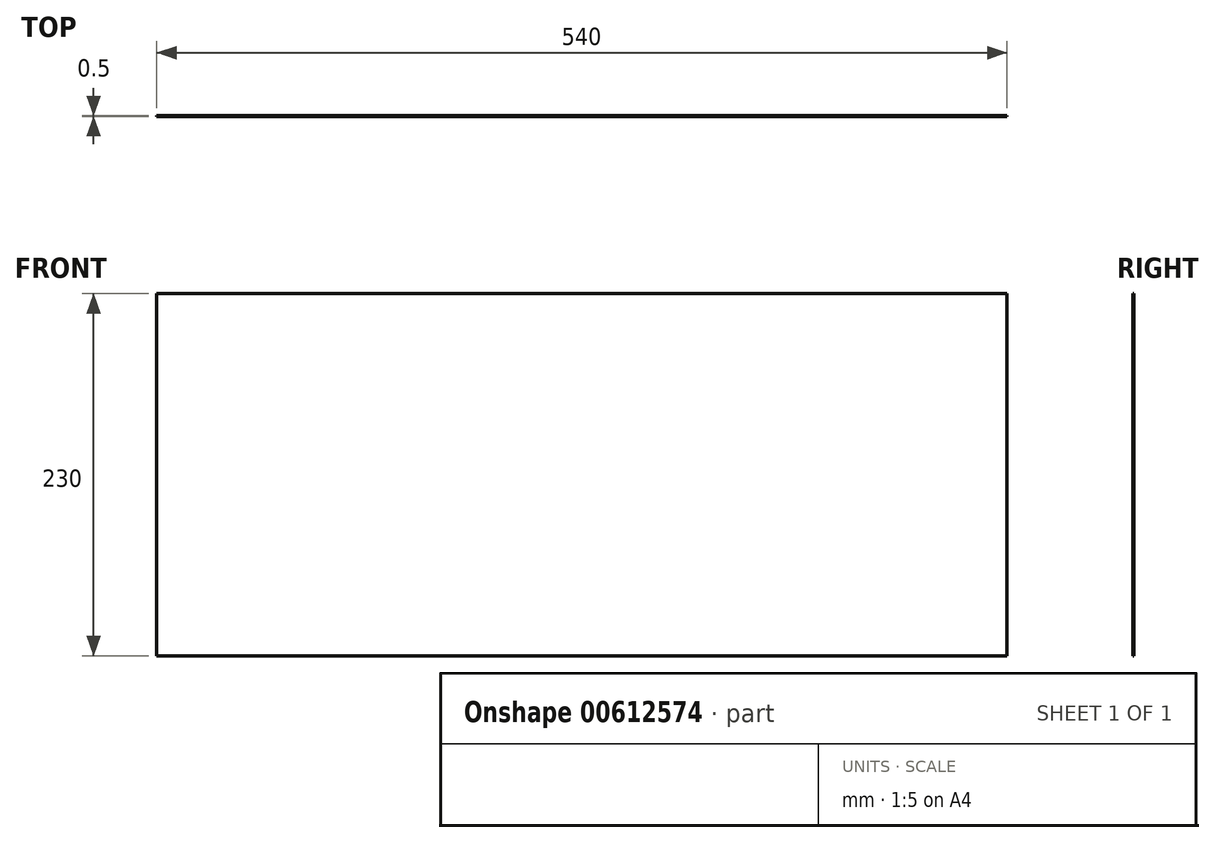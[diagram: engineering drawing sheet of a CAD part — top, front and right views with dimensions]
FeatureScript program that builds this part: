
annotation { "Feature Type Name" : "Feature", "Feature Type Description" : "" }
export const myFeature = defineFeature(function(context is Context, id is Id, definition is map)
    precondition{}
    {
        {
            var Q0;
            Q0=qCreatedBy(makeId("Front.planeOp"),FACE);
            var sketch = newSketch(context, id + "F0", { "sketchPlane" : qUnion([Q0])});
            skLineSegment(sketch, "E0.bottom", {"start": v(-270, 115) * mm, "end": v(270, 115) * mm});
            skLineSegment(sketch, "E0.top", {"start": v(-270, -115) * mm, "end": v(270, -115) * mm});
            skLineSegment(sketch, "E0.left", {"start": v(-270, 115) * mm, "end": v(-270, -115) * mm});
            skLineSegment(sketch, "E0.right", {"start": v(270, 115) * mm, "end": v(270, -115) * mm});
            skPoint(sketch, "E0.middle", {"position": v(0, 0) * mm});
            skSolve(sketch);
        }
        {
            var Q0;
            Q0=makeQuery(id+"F0.imprint","IMPRINT",FACE,{"disambiguationData":[TD([[makeQuery(id+"F0.imprint","IMPRINT",EDGE,{"derivedFrom":sQuery(id+"F0.wireOp",EDGE,"E0.bottom")}),-1.0]])]});
            extrude(context, id + "F1", {"entities" : qUnion([Q0]), "depth" : 0.5 * mm, "offsetDistance" : 25.4 * mm});
        }
    });
